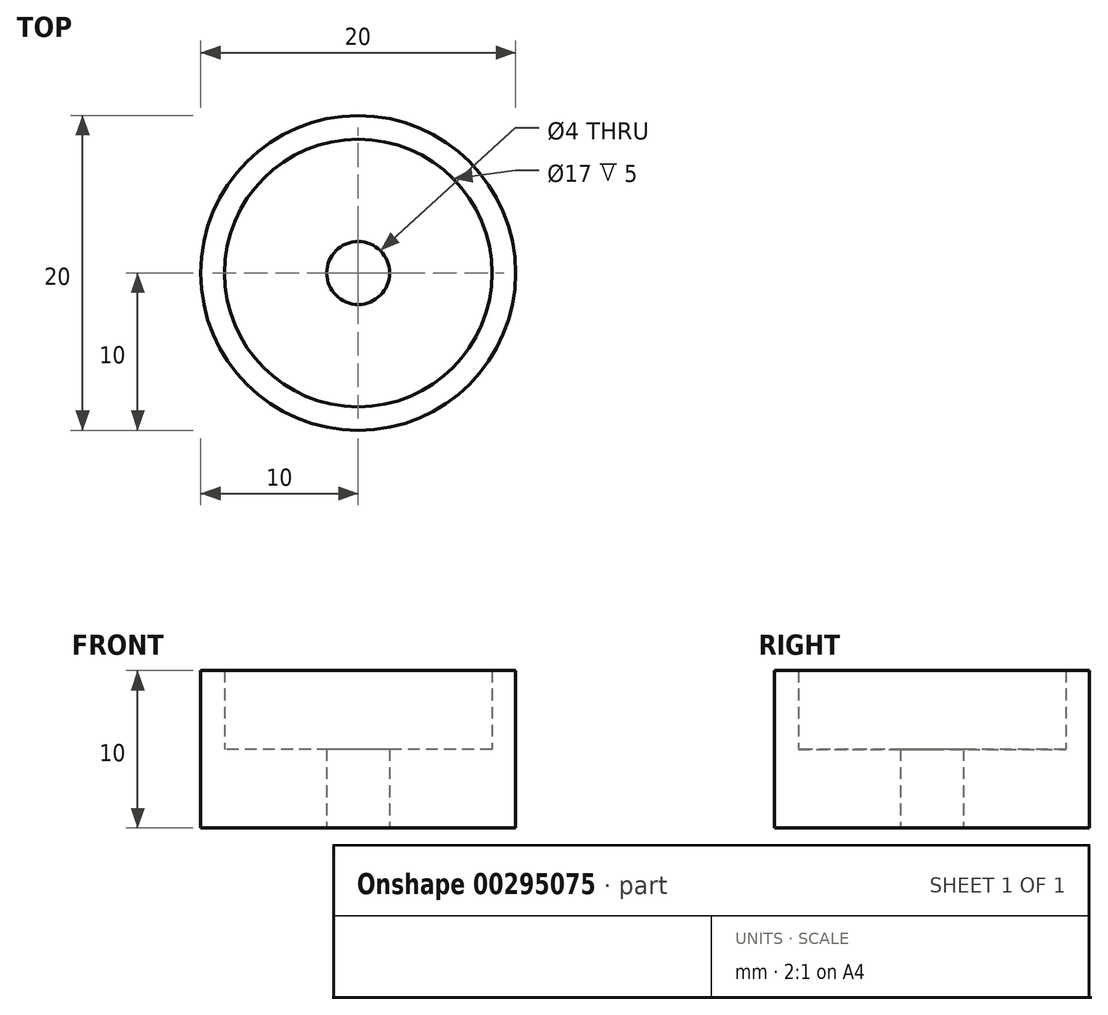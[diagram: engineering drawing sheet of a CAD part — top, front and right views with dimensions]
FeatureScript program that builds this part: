
annotation { "Feature Type Name" : "Feature", "Feature Type Description" : "" }
export const myFeature = defineFeature(function(context is Context, id is Id, definition is map)
    precondition{}
    {
        {
            var Q0;
            Q0=qCreatedBy(makeId("Top.planeOp"),FACE);
            var sketch = newSketch(context, id + "F0", { "sketchPlane" : qUnion([Q0])});
            skCircle(sketch, "E0", {"center": v(0, 0) * mm, "radius": 10 * mm});
            skCircle(sketch, "E1", {"center": v(0, 0) * mm, "radius": 2 * mm});
            skSolve(sketch);
        }
        {
            var Q0;
            Q0 = qSketchRegion(id + "F0", true);
            extrude(context, id + "F1", {"entities" : qUnion([Q0]), "depth" : 5 * mm});
        }
        {
            var Q0;
            Q0=makeQuery(id+"F1.opExtrude","CAP_FACE",FACE,{"disambiguationData":[OSD([sQuery(id+"F0.wireOp",EDGE,"E0"),sQuery(id+"F0.wireOp",EDGE,"E1")])],"isStart":false});
            var sketch = newSketch(context, id + "F2", { "sketchPlane" : qUnion([Q0])});
            skCircle(sketch, "E2", {"center": v(0, 0) * mm, "radius": 8.5 * mm});
            skSolve(sketch);
        }
        {
            var Q0;
            Q0=makeQuery(id+"F2.imprint","IMPRINT",FACE,{"disambiguationData":[TD([[makeQuery(id+"F2.imprint","IMPRINT",EDGE,{"derivedFrom":sQuery(id+"F2.wireOp",EDGE,"E2")}),-1.0]])]});
            extrude(context, id + "F3", {"entities" : qUnion([Q0]), "operationType" : NewBodyOperationType.ADD, "depth" : 5 * mm});
        }
    });
